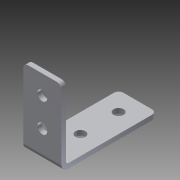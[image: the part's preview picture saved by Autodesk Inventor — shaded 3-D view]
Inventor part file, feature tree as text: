
AUTODESK INVENTOR PART (.ipt)
format: ipt  version: 2013 (Build 170138000, 138)  size: 182,272 bytes
history: native  units: in
note: dims shown in document units (in); Inventor stores cm internally (conversion verified against a paired STEP export)
features: sheet_metal_op x4, other x4, sketch x3, chamfer x1
ambient origin geometry x8: Origin, YZ Plane, XZ Plane, XY Plane, X Axis, Y Axis, Z Axis, Center Point
bodies: Solid1 (feature_tree)
feature tree (12):
  sheet_metal_op  "Face1"
  sheet_metal_op  "Flange1"
  chamfer  "Corner Round1"
  sketch  "Sketch1"  dims[d0=0.26in]
  other  "Plate1"
  sketch  "Sketch2"  dims[d2=1.0in]
  other  "Plate2"
  sheet_metal_op  "Bend1"
  sheet_metal_op  "Corner1"
  sketch  "Sketch3"  dims[d3=2.5in d4=1.0in d5=1.0in d6=0.125in d7=0.125in d8=0.0625in d9=0.25in d10=0.125in d11=2.0in d12=90.0deg d13=0.05in d14=0.5in d15=0.125in d16=0.125in d17=0.75in d18=0.75in d19=0.26in d20=0.125in d21=0.0in d22=0.125in]
  other  "Cut1"
  other  "Definition1"
